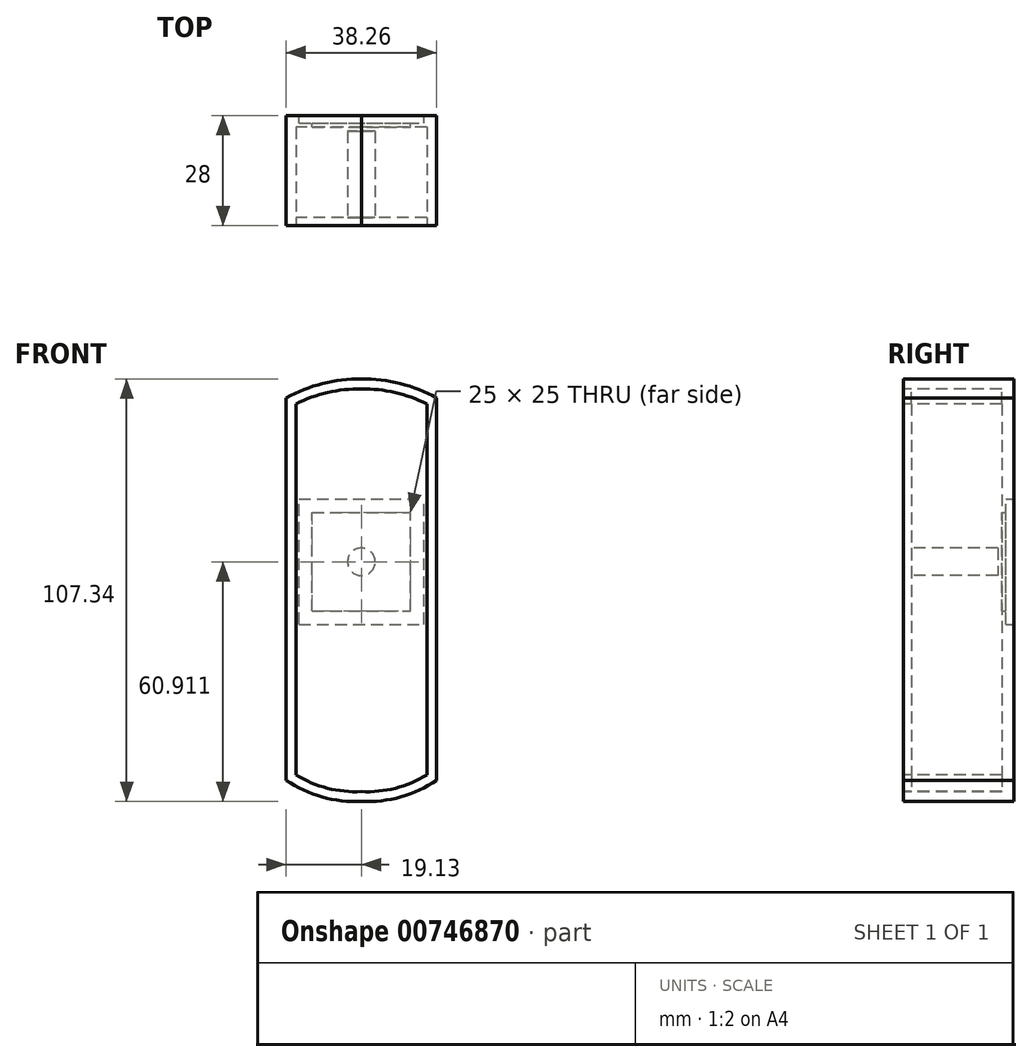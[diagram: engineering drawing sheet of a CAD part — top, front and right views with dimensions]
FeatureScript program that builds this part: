
annotation { "Feature Type Name" : "Feature", "Feature Type Description" : "" }
export const myFeature = defineFeature(function(context is Context, id is Id, definition is map)
    precondition{}
    {
        {
            var Q0;
            Q0=qCreatedBy(makeId("Right.planeOp"),FACE);
            var sketch = newSketch(context, id + "F0", { "sketchPlane" : qUnion([Q0])});
            skLineSegment(sketch, "E0", {"start": v(0, 0) * mm, "end": v(-0.02, -102.3) * mm, "construction": true});
            skSolve(sketch);
        }
        {
            var Q0;
            Q0=qCreatedBy(makeId("Front.planeOp"),FACE);
            var sketch = newSketch(context, id + "F1", { "sketchPlane" : qUnion([Q0])});
            skLineSegment(sketch, "E1.0", {"start": v(0, 0) * mm, "end": v(0, -102.3) * mm, "construction": true});
            skLineSegment(sketch, "E2", {"start": v(16.62, -3.8) * mm, "end": v(16.63, -98.07) * mm});
            skArc(sketch, "E3", {"start": v(16.62, -3.8) * mm, "mid": v(8.54, -0.9) * mm, "end": v(0, 0) * mm});
            skPoint(sketch, "E4.orphan", {"position": v(-15.58, -3.8) * mm});
            skArc(sketch, "E5", {"start": v(0, -102.3) * mm, "mid": v(8.63, -101.45) * mm, "end": v(16.63, -98.07) * mm});
            skPoint(sketch, "E6.orphan", {"position": v(-13.6, -98.07) * mm});
            skArc(sketch, "E7.MirrorCS", {"start": v(-16.62, -3.8) * mm, "mid": v(-8.54, -0.9) * mm, "end": v(0, 0) * mm});
            skLineSegment(sketch, "E8.MirrorCS", {"start": v(-16.62, -3.8) * mm, "end": v(-16.62, -98.07) * mm});
            skArc(sketch, "E9.MirrorCS", {"start": v(0, -102.3) * mm, "mid": v(-8.63, -101.45) * mm, "end": v(-16.63, -98.07) * mm});
            skSolve(sketch);
        }
        {
            var Q0;
            Q0 = qSketchRegion(id + "F1", true);
            extrude(context, id + "F2", {"entities" : qUnion([Q0]), "oppositeDirection" : true, "depth" : 2 * mm, "offsetDistance" : 25 * mm});
        }
        {
            var Q0;
            Q0=makeQuery(id+"F2.opExtrude","CAP_FACE",FACE,{"disambiguationData":[OSD([sQuery(id+"F1.wireOp",EDGE,"E2"),sQuery(id+"F1.wireOp",EDGE,"E3"),sQuery(id+"F1.wireOp",EDGE,"E5"),sQuery(id+"F1.wireOp",EDGE,"E7.MirrorCS"),sQuery(id+"F1.wireOp",EDGE,"E8.MirrorCS"),sQuery(id+"F1.wireOp",EDGE,"E9.MirrorCS")])],"isStart":false});
            var sketch = newSketch(context, id + "F3", { "sketchPlane" : qUnion([Q0])});
            skCircle(sketch, "E10", {"center": v(0, -43.93) * mm, "radius": 3.5 * mm});
            skSolve(sketch);
        }
        {
            var Q0;
            Q0 = qSketchRegion(id + "F3", true);
            extrude(context, id + "F4", {"entities" : qUnion([Q0]), "operationType" : NewBodyOperationType.ADD, "depth" : 22 * mm, "offsetDistance" : 25 * mm});
        }
        {
            var Q0;
            Q0=makeQuery(id+"F2.opExtrude","CAP_FACE",FACE,{"disambiguationData":[OSD([sQuery(id+"F1.wireOp",EDGE,"E2"),sQuery(id+"F1.wireOp",EDGE,"E3"),sQuery(id+"F1.wireOp",EDGE,"E5"),sQuery(id+"F1.wireOp",EDGE,"E7.MirrorCS"),sQuery(id+"F1.wireOp",EDGE,"E8.MirrorCS"),sQuery(id+"F1.wireOp",EDGE,"E9.MirrorCS")])],"isStart":true});
            var sketch = newSketch(context, id + "F5", { "sketchPlane" : qUnion([Q0])});
            skArc(sketch, "E11.0.0", {"start": v(0, -102.3) * mm, "mid": v(-8.63, -101.45) * mm, "end": v(-16.63, -98.07) * mm});
            skLineSegment(sketch, "E11.0.1", {"start": v(-16.62, -98.07) * mm, "end": v(-16.62, -3.8) * mm});
            skArc(sketch, "E11.0.2", {"start": v(-16.62, -3.8) * mm, "mid": v(-8.54, -0.9) * mm, "end": v(0, 0) * mm});
            skArc(sketch, "E11.0.3", {"start": v(0, 0) * mm, "mid": v(8.54, -0.9) * mm, "end": v(16.62, -3.8) * mm});
            skLineSegment(sketch, "E11.0.4", {"start": v(16.62, -3.8) * mm, "end": v(16.63, -98.07) * mm});
            skArc(sketch, "E11.0.5", {"start": v(16.63, -98.07) * mm, "mid": v(8.63, -101.45) * mm, "end": v(0, -102.3) * mm});
            skArc(sketch, "E12.0", {"start": v(19.13, -99.44) * mm, "mid": v(10, -103.67) * mm, "end": v(0, -104.8) * mm});
            skLineSegment(sketch, "E12.1", {"start": v(-19.13, -99.44) * mm, "end": v(-19.13, -2.29) * mm});
            skArc(sketch, "E12.2", {"start": v(-19.13, -2.29) * mm, "mid": v(-9.87, 1.35) * mm, "end": v(0, 2.5) * mm});
            skArc(sketch, "E12.3", {"start": v(0, -104.8) * mm, "mid": v(-10, -103.67) * mm, "end": v(-19.13, -99.44) * mm});
            skArc(sketch, "E12.4", {"start": v(0, 2.5) * mm, "mid": v(9.87, 1.35) * mm, "end": v(19.13, -2.29) * mm});
            skLineSegment(sketch, "E12.5", {"start": v(19.12, -2.29) * mm, "end": v(19.13, -99.44) * mm});
            skSolve(sketch);
        }
        {
            var Q0;
            Q0 = qSketchRegion(id + "F5", true);
            extrude(context, id + "F6", {"entities" : qUnion([Q0]), "oppositeDirection" : true, "depth" : 25 * mm, "offsetDistance" : 25 * mm});
        }
        {
            var Q0;
            Q0=makeQuery(id+"F6.opExtrude","CAP_FACE",FACE,{"disambiguationData":[OSD([sQuery(id+"F5.wireOp",EDGE,"E11.0.0"),sQuery(id+"F5.wireOp",EDGE,"E11.0.1"),sQuery(id+"F5.wireOp",EDGE,"E11.0.2"),sQuery(id+"F5.wireOp",EDGE,"E11.0.3"),sQuery(id+"F5.wireOp",EDGE,"E11.0.4"),sQuery(id+"F5.wireOp",EDGE,"E11.0.5"),sQuery(id+"F5.wireOp",EDGE,"E12.0"),sQuery(id+"F5.wireOp",EDGE,"E12.1"),sQuery(id+"F5.wireOp",EDGE,"E12.2"),sQuery(id+"F5.wireOp",EDGE,"E12.3"),sQuery(id+"F5.wireOp",EDGE,"E12.4"),sQuery(id+"F5.wireOp",EDGE,"E12.5")])],"isStart":false});
            var sketch = newSketch(context, id + "F7", { "sketchPlane" : qUnion([Q0])});
            skArc(sketch, "E13.0.0", {"start": v(0, 2.5) * mm, "mid": v(-9.87, 1.35) * mm, "end": v(-19.12, -2.29) * mm});
            skLineSegment(sketch, "E13.0.1", {"start": v(-19.12, -2.29) * mm, "end": v(-19.13, -99.44) * mm});
            skArc(sketch, "E13.0.2", {"start": v(-19.13, -99.44) * mm, "mid": v(-10, -103.67) * mm, "end": v(0, -104.8) * mm});
            skArc(sketch, "E13.0.3", {"start": v(0, -104.8) * mm, "mid": v(10, -103.67) * mm, "end": v(19.13, -99.44) * mm});
            skLineSegment(sketch, "E13.0.4", {"start": v(19.13, -99.44) * mm, "end": v(19.13, -2.29) * mm});
            skArc(sketch, "E13.0.5", {"start": v(19.13, -2.29) * mm, "mid": v(9.87, 1.35) * mm, "end": v(0, 2.5) * mm});
            skSolve(sketch);
        }
        {
            var Q0;
            Q0 = qSketchRegion(id + "F7", true);
            extrude(context, id + "F8", {"entities" : qUnion([Q0]), "operationType" : NewBodyOperationType.ADD, "depth" : 3 * mm, "offsetDistance" : 25 * mm});
        }
        {
            var Q0;
            Q0=makeQuery(id+"F8.opExtrude","CAP_FACE",FACE,{"disambiguationData":[OSD([sQuery(id+"F7.wireOp",EDGE,"E13.0.0"),sQuery(id+"F7.wireOp",EDGE,"E13.0.1"),sQuery(id+"F7.wireOp",EDGE,"E13.0.2"),sQuery(id+"F7.wireOp",EDGE,"E13.0.3"),sQuery(id+"F7.wireOp",EDGE,"E13.0.4"),sQuery(id+"F7.wireOp",EDGE,"E13.0.5")])],"isStart":false});
            var sketch = newSketch(context, id + "F9", { "sketchPlane" : qUnion([Q0])});
            skLineSegment(sketch, "E14.bottom", {"start": v(12.5, -56.43) * mm, "end": v(-12.5, -56.43) * mm});
            skLineSegment(sketch, "E14.top", {"start": v(12.5, -31.43) * mm, "end": v(-12.5, -31.43) * mm});
            skLineSegment(sketch, "E14.left", {"start": v(12.5, -56.43) * mm, "end": v(12.5, -31.43) * mm});
            skLineSegment(sketch, "E14.right", {"start": v(-12.5, -56.43) * mm, "end": v(-12.5, -31.43) * mm});
            skPoint(sketch, "E14.middle", {"position": v(0, -43.93) * mm});
            skSolve(sketch);
        }
        {
            var Q0;
            Q0 = qSketchRegion(id + "F9", true);
            extrude(context, id + "F10", {"entities" : qUnion([Q0]), "operationType" : NewBodyOperationType.REMOVE, "oppositeDirection" : true, "depth" : 3 * mm, "offsetDistance" : 25 * mm});
        }
        {
            var Q0;
            Q0=makeQuery(id+"F8.opExtrude","CAP_FACE",FACE,{"disambiguationData":[OSD([sQuery(id+"F7.wireOp",EDGE,"E13.0.0"),sQuery(id+"F7.wireOp",EDGE,"E13.0.1"),sQuery(id+"F7.wireOp",EDGE,"E13.0.2"),sQuery(id+"F7.wireOp",EDGE,"E13.0.3"),sQuery(id+"F7.wireOp",EDGE,"E13.0.4"),sQuery(id+"F7.wireOp",EDGE,"E13.0.5")])],"isStart":false});
            var sketch = newSketch(context, id + "F11", { "sketchPlane" : qUnion([Q0])});
            skLineSegment(sketch, "E15.0", {"start": v(12.5, -31.43) * mm, "end": v(-12.5, -31.43) * mm});
            skLineSegment(sketch, "E16.0", {"start": v(-12.5, -56.43) * mm, "end": v(-12.5, -31.43) * mm});
            skLineSegment(sketch, "E17.0", {"start": v(12.5, -56.43) * mm, "end": v(-12.5, -56.43) * mm});
            skLineSegment(sketch, "E18.0", {"start": v(12.5, -56.43) * mm, "end": v(12.5, -31.43) * mm});
            skLineSegment(sketch, "E19.0", {"start": v(15.9, -28.03) * mm, "end": v(-15.9, -28.03) * mm});
            skLineSegment(sketch, "E19.1", {"start": v(15.9, -59.83) * mm, "end": v(15.9, -28.03) * mm});
            skLineSegment(sketch, "E19.2", {"start": v(15.9, -59.83) * mm, "end": v(-15.9, -59.83) * mm});
            skLineSegment(sketch, "E19.3", {"start": v(-15.9, -59.83) * mm, "end": v(-15.9, -28.03) * mm});
            skSolve(sketch);
        }
        {
            var Q0;
            Q0 = qSketchRegion(id + "F11", true);
            extrude(context, id + "F12", {"entities" : qUnion([Q0]), "operationType" : NewBodyOperationType.REMOVE, "oppositeDirection" : true, "depth" : 2 * mm, "offsetDistance" : 25 * mm});
        }
    });
